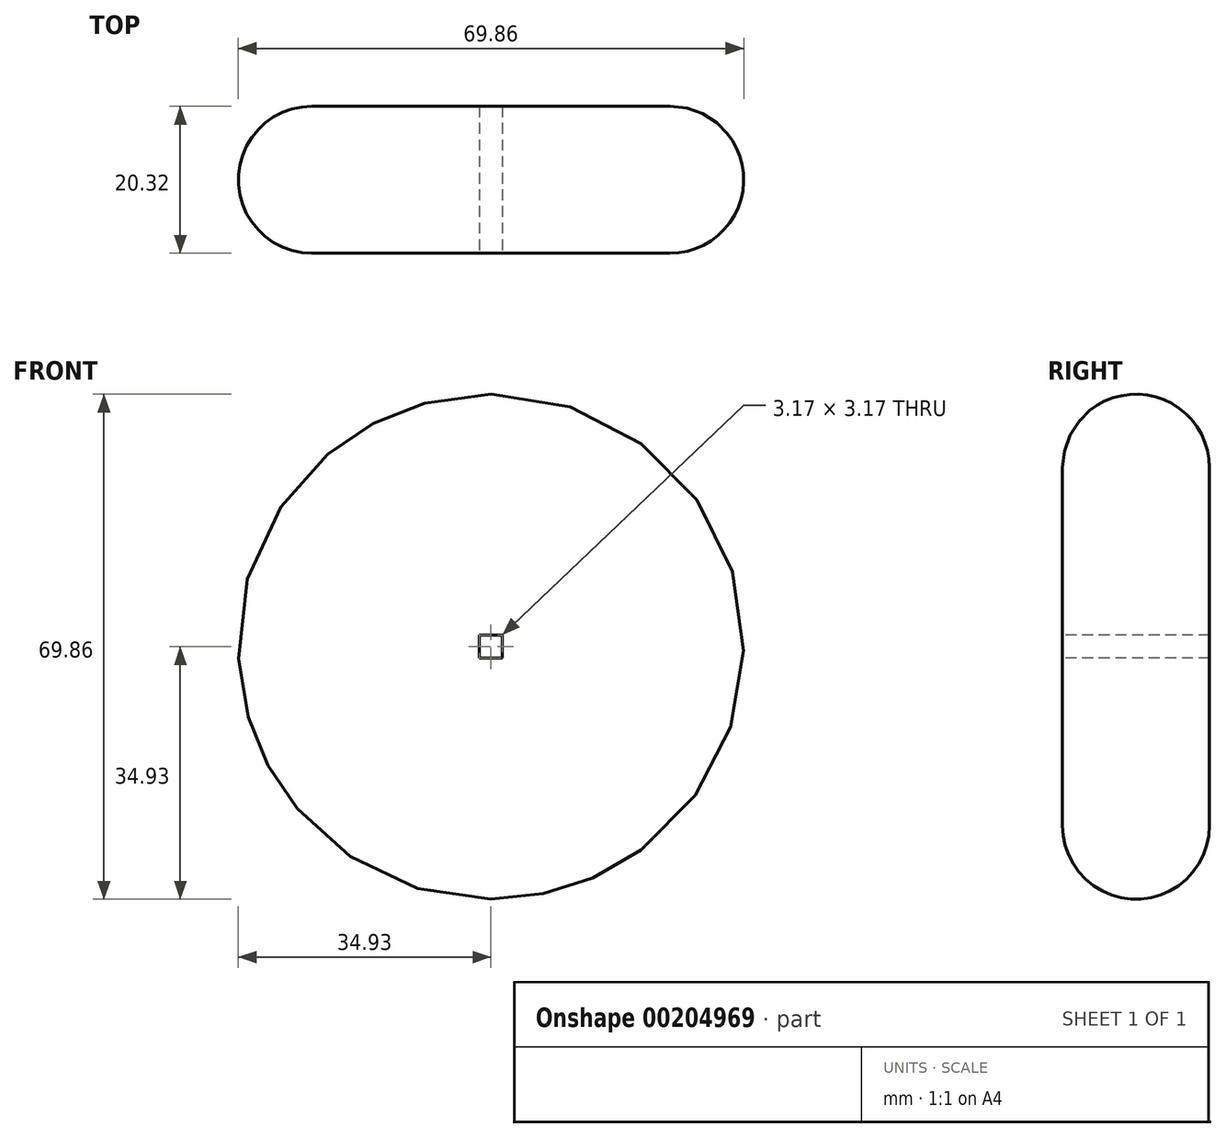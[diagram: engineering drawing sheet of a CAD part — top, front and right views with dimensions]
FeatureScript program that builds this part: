
annotation { "Feature Type Name" : "Feature", "Feature Type Description" : "" }
export const myFeature = defineFeature(function(context is Context, id is Id, definition is map)
    precondition{}
    {
        {
            var Q0;
            Q0=qCreatedBy(makeId("Front.planeOp"),FACE);
            var sketch = newSketch(context, id + "F0", { "sketchPlane" : qUnion([Q0])});
            skCircle(sketch, "E0", {"center": v(0, 0) * mm, "radius": 34.93 * mm});
            skSolve(sketch);
        }
        {
            var Q0;
            Q0 = qSketchRegion(id + "F0", true);
            extrude(context, id + "F1", {"entities" : qUnion([Q0]), "depth" : 20.32 * mm});
        }
        {
            var Q0;
            Q0=makeQuery(id+"F1.opExtrude","CAP_EDGE",EDGE,{"disambiguationData":[OSD([sQuery(id+"F0.wireOp",EDGE,"E0")])],"isStart":false});
            var Q1;
            Q1=makeQuery(id+"F1.opExtrude","CAP_EDGE",EDGE,{"disambiguationData":[OSD([sQuery(id+"F0.wireOp",EDGE,"E0")])],"isStart":true});
            fillet(context, id + "F2", {"entities" : qUnion([Q0, Q1]), "radius" : 10.16 * mm, "tangentPropagation" : true, "allowEdgeOverflow" : false});
        }
        {
            var Q0;
            Q0=makeQuery(id+"F1.opExtrude","CAP_FACE",FACE,{"disambiguationData":[OSD([sQuery(id+"F0.wireOp",EDGE,"E0")])],"isStart":false});
            var sketch = newSketch(context, id + "F3", { "sketchPlane" : qUnion([Q0])});
            skLineSegment(sketch, "E1.bottom", {"start": v(1.59, -1.59) * mm, "end": v(-1.59, -1.59) * mm});
            skLineSegment(sketch, "E1.top", {"start": v(1.59, 1.59) * mm, "end": v(-1.59, 1.59) * mm});
            skLineSegment(sketch, "E1.left", {"start": v(1.59, -1.59) * mm, "end": v(1.59, 1.59) * mm});
            skLineSegment(sketch, "E1.right", {"start": v(-1.59, -1.59) * mm, "end": v(-1.59, 1.59) * mm});
            skPoint(sketch, "E1.middle", {"position": v(0, 0) * mm});
            skSolve(sketch);
        }
        {
            var Q0;
            Q0=makeQuery(id+"F3.imprint","IMPRINT",FACE,{"disambiguationData":[TD([[makeQuery(id+"F3.imprint","IMPRINT",EDGE,{"derivedFrom":sQuery(id+"F3.wireOp",EDGE,"E1.bottom")}),-1.0]])]});
            extrude(context, id + "F4", {"entities" : qUnion([Q0]), "operationType" : NewBodyOperationType.REMOVE, "endBound" : BoundingType.UP_TO_NEXT, "oppositeDirection" : true, "depth" : 25.4 * mm});
        }
    });
